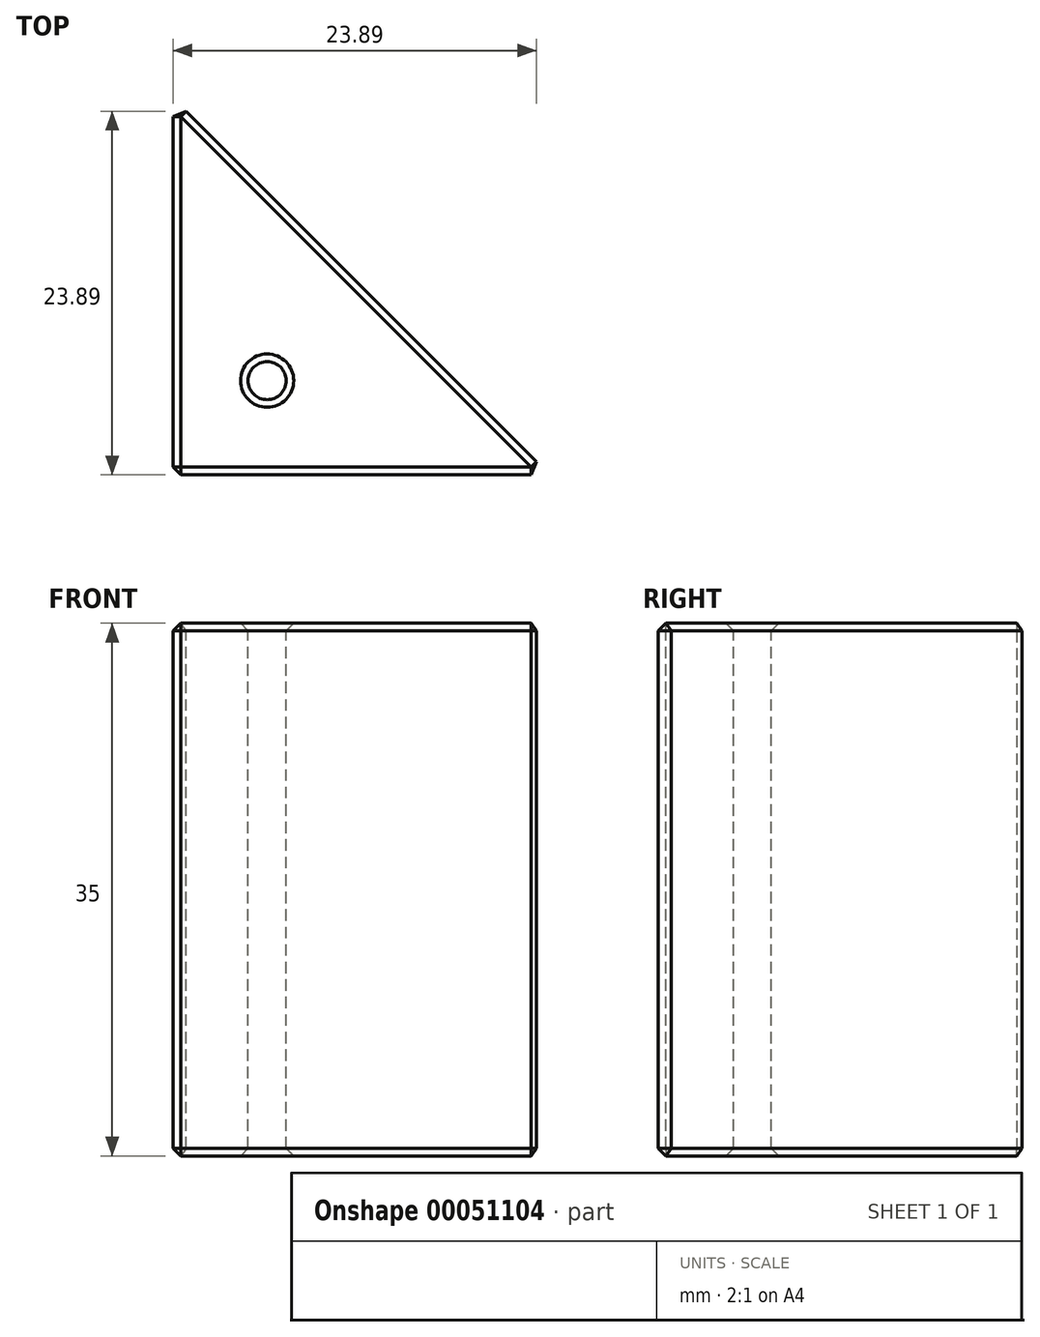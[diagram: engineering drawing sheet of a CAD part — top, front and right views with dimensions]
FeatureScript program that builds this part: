
annotation { "Feature Type Name" : "Feature", "Feature Type Description" : "" }
export const myFeature = defineFeature(function(context is Context, id is Id, definition is map)
    precondition{}
    {
        {
            var Q0;
            Q0=qCreatedBy(makeId("Top.planeOp"),FACE);
            var sketch = newSketch(context, id + "F0", { "sketchPlane" : qUnion([Q0])});
            skLineSegment(sketch, "E0.bottom", {"start": v(0, 0) * mm, "end": v(24.75, 0) * mm});
            skLineSegment(sketch, "E0.top", {"start": v(0, 24.75) * mm, "end": v(24.75, 24.75) * mm});
            skLineSegment(sketch, "E0.left", {"start": v(0, 0) * mm, "end": v(0, 24.75) * mm});
            skLineSegment(sketch, "E0.right", {"start": v(24.75, 0) * mm, "end": v(24.75, 24.75) * mm});
            skSolve(sketch);
        }
        {
            var Q0;
            Q0=makeQuery(id+"F0.imprint","IMPRINT",FACE,{"disambiguationData":[TD([[makeQuery(id+"F0.imprint","IMPRINT",EDGE,{"derivedFrom":sQuery(id+"F0.wireOp",EDGE,"E0.bottom")}),1.0]])]});
            extrude(context, id + "F1", {"entities" : qUnion([Q0]), "depth" : 35 * mm});
        }
        {
            var Q0;
            Q0=makeQuery(id+"F1.opExtrude","CAP_FACE",FACE,{"disambiguationData":[OSD([sQuery(id+"F0.wireOp",EDGE,"E0.bottom"),sQuery(id+"F0.wireOp",EDGE,"E0.top"),sQuery(id+"F0.wireOp",EDGE,"E0.left"),sQuery(id+"F0.wireOp",EDGE,"E0.right")])],"isStart":false});
            var sketch = newSketch(context, id + "F2", { "sketchPlane" : qUnion([Q0])});
            skLineSegment(sketch, "E1", {"start": v(0, 24.75) * mm, "end": v(24.75, 24.75) * mm});
            skLineSegment(sketch, "E2", {"start": v(24.75, 24.75) * mm, "end": v(24.75, 0) * mm});
            skLineSegment(sketch, "E3", {"start": v(24.75, 0) * mm, "end": v(0, 24.75) * mm});
            skSolve(sketch);
        }
        {
            var Q0;
            Q0=makeQuery(id+"F2.imprint","IMPRINT",FACE,{"disambiguationData":[TD([[makeQuery(id+"F2.imprint","IMPRINT",EDGE,{"derivedFrom":sQuery(id+"F2.wireOp",EDGE,"E1")}),-1.0]])]});
            extrude(context, id + "F3", {"entities" : qUnion([Q0]), "operationType" : NewBodyOperationType.REMOVE, "oppositeDirection" : true, "depth" : 35 * mm});
        }
        {
            var Q0;
            Q0=makeQuery(id+"F1.opExtrude","CAP_FACE",FACE,{"disambiguationData":[OSD([sQuery(id+"F0.wireOp",EDGE,"E0.bottom"),sQuery(id+"F0.wireOp",EDGE,"E0.top"),sQuery(id+"F0.wireOp",EDGE,"E0.left"),sQuery(id+"F0.wireOp",EDGE,"E0.right")])],"isStart":false});
            var sketch = newSketch(context, id + "F4", { "sketchPlane" : qUnion([Q0])});
            skCircle(sketch, "E4", {"center": v(6.19, 6.19) * mm, "radius": 1.25 * mm});
            skSolve(sketch);
        }
        {
            var Q0;
            Q0 = qSketchRegion(id + "F4", true);
            extrude(context, id + "F5", {"entities" : qUnion([Q0]), "operationType" : NewBodyOperationType.REMOVE, "oppositeDirection" : true, "depth" : 35 * mm});
        }
        {
            var Q0;
            Q0=makeQuery(id+"F1.opExtrude","CAP_FACE",FACE,{"disambiguationData":[OSD([sQuery(id+"F0.wireOp",EDGE,"E0.bottom"),sQuery(id+"F0.wireOp",EDGE,"E0.top"),sQuery(id+"F0.wireOp",EDGE,"E0.left"),sQuery(id+"F0.wireOp",EDGE,"E0.right")])],"isStart":false});
            var Q1;
            Q1=makeQuery(id+"F3.boolean.opBoolean","COPY",FACE,{"derivedFrom":makeQuery(id+"F3.opExtrude","SWEPT_FACE",FACE,{"disambiguationData":[OSD([sQuery(id+"F2.wireOp",EDGE,"E3")])]})});
            var Q2;
            Q2=makeQuery(id+"F1.opExtrude","SWEPT_FACE",FACE,{"disambiguationData":[OSD([sQuery(id+"F0.wireOp",EDGE,"E0.bottom")])]});
            var Q3;
            Q3=makeQuery(id+"F1.opExtrude","SWEPT_FACE",FACE,{"disambiguationData":[OSD([sQuery(id+"F0.wireOp",EDGE,"E0.left")])]});
            var Q4;
            Q4=makeQuery(id+"F1.opExtrude","CAP_FACE",FACE,{"disambiguationData":[OSD([sQuery(id+"F0.wireOp",EDGE,"E0.bottom"),sQuery(id+"F0.wireOp",EDGE,"E0.top"),sQuery(id+"F0.wireOp",EDGE,"E0.left"),sQuery(id+"F0.wireOp",EDGE,"E0.right")])],"isStart":true});
            chamfer(context, id + "F6", {"entities" : qUnion([Q0, Q1, Q2, Q3, Q4]), "width" : 0.5 * mm, "tangentPropagation" : true});
        }
    });
